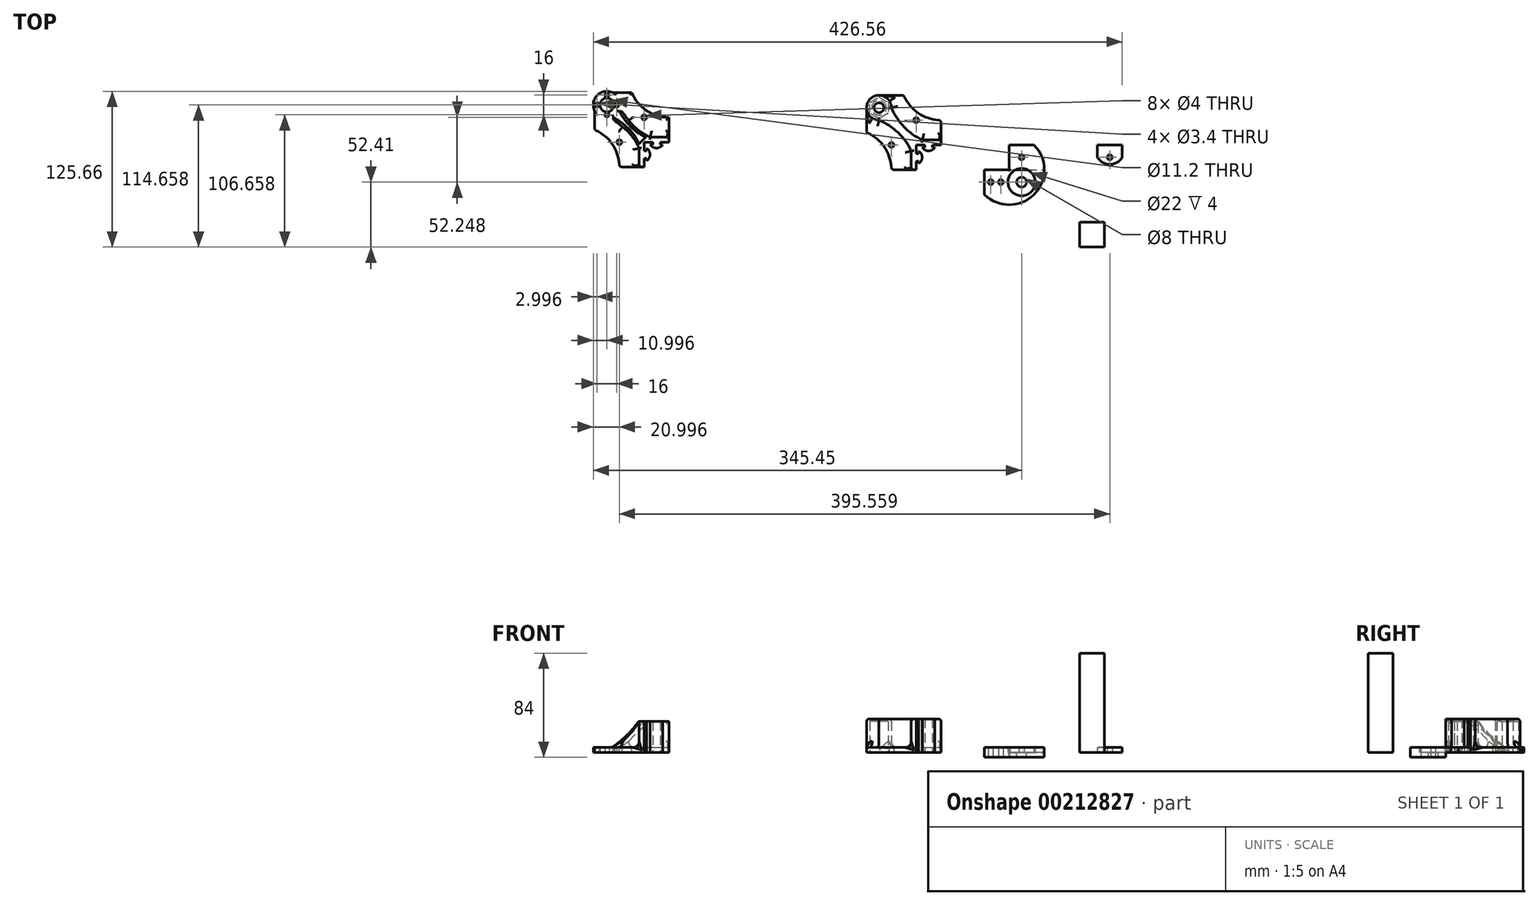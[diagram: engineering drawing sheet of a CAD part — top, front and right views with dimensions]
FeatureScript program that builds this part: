
annotation { "Feature Type Name" : "Feature", "Feature Type Description" : "" }
export const myFeature = defineFeature(function(context is Context, id is Id, definition is map)
    precondition{}
    {
        {
            var Q0;
            Q0=qCreatedBy(makeId("Top.planeOp"),FACE);
            var sketch = newSketch(context, id + "F0", { "sketchPlane" : qUnion([Q0])});
            skLineSegment(sketch, "E0.top", {"start": v(9.5, -10) * mm, "end": v(-10, -10) * mm});
            skLineSegment(sketch, "E0.left", {"start": v(10, 10) * mm, "end": v(10, -9.5) * mm});
            skPoint(sketch, "E0.middle", {"position": v(0, 0) * mm});
            skLineSegment(sketch, "E1.bottom", {"start": v(-10, -10) * mm, "end": v(-30, -10) * mm});
            skLineSegment(sketch, "E1.top", {"start": v(-10, -30) * mm, "end": v(-30, -30) * mm});
            skLineSegment(sketch, "E1.left", {"start": v(-10, -10) * mm, "end": v(-10, -30) * mm});
            skLineSegment(sketch, "E1.right", {"start": v(-30, -10) * mm, "end": v(-30, -30) * mm});
            skLineSegment(sketch, "E2.bottom", {"start": v(10, 10) * mm, "end": v(30, 10) * mm, "construction": true});
            skLineSegment(sketch, "E2.top", {"start": v(10, 30) * mm, "end": v(30, 30) * mm});
            skLineSegment(sketch, "E2.left", {"start": v(10, 10) * mm, "end": v(10, 30) * mm});
            skLineSegment(sketch, "E2.right", {"start": v(30, 10) * mm, "end": v(30, 30) * mm});
            skLineSegment(sketch, "E3", {"start": v(-10, -30) * mm, "end": v(10, -30) * mm});
            skLineSegment(sketch, "E4", {"start": v(10, -10) * mm, "end": v(30, -30) * mm, "construction": true});
            skCircle(sketch, "E5", {"center": v(20, -20) * mm, "radius": 4 * mm});
            skCircle(sketch, "E6", {"center": v(20, -20) * mm, "radius": 11 * mm});
            skLineSegment(sketch, "E7", {"start": v(-10, -30) * mm, "end": v(-30, -10) * mm, "construction": true});
            skLineSegment(sketch, "E8", {"start": v(30, 10) * mm, "end": v(10, 30) * mm, "construction": true});
            skCircle(sketch, "E9", {"center": v(20, 20) * mm, "radius": 2 * mm});
            skCircle(sketch, "E10", {"center": v(-20, -20) * mm, "radius": 2 * mm});
            skLineSegment(sketch, "E11", {"start": v(30, -10) * mm, "end": v(30, 10) * mm});
            skArc(sketch, "E12", {"start": v(10, -30) * mm, "mid": v(30, -30) * mm, "end": v(30, -10) * mm, "construction": true});
            skArc(sketch, "E13", {"start": v(9.5, -10) * mm, "mid": v(10.35, -10.35) * mm, "end": v(10, -9.5) * mm});
            skCircle(sketch, "E14", {"center": v(20, 0) * mm, "radius": 2 * mm});
            skPoint(sketch, "E14.centerSnap0", {"position": v(20, 10) * mm});
            skCircle(sketch, "E15", {"center": v(3.25, -20) * mm, "radius": 2 * mm});
            skPoint(sketch, "E15.centerSnap0", {"position": v(-10, -20) * mm});
            skLineSegment(sketch, "E16", {"start": v(55.55, 30) * mm, "end": v(55.55, -7.44) * mm, "construction": true});
            skLineSegment(sketch, "E17.MirrorCS", {"start": v(81.1, 0.25) * mm, "end": v(81.1, 10) * mm});
            skCircle(sketch, "E18.MirrorC", {"center": v(91.1, 0) * mm, "radius": 2 * mm});
            skLineSegment(sketch, "E19.MirrorCS", {"start": v(81.1, 10) * mm, "end": v(81.1, 30) * mm, "construction": true});
            skLineSegment(sketch, "E20.MirrorCS", {"start": v(101.1, 0.25) * mm, "end": v(101.1, 30) * mm});
            skLineSegment(sketch, "E21.MirrorCS", {"start": v(101.1, 30) * mm, "end": v(81.1, 30) * mm, "construction": true});
            skCircle(sketch, "E22.MirrorC", {"center": v(91.1, 20) * mm, "radius": 2 * mm});
            skArc(sketch, "E23", {"start": v(81.1, 0.25) * mm, "mid": v(91.1, -5.73) * mm, "end": v(101.1, 0.25) * mm});
            skPoint(sketch, "E24.MirrorCS.start.orphan", {"position": v(101.1, 10) * mm});
            skLineSegment(sketch, "E25.left", {"start": v(-3, 8) * mm, "end": v(-3, 10) * mm});
            skLineSegment(sketch, "E25.right", {"start": v(3, 8) * mm, "end": v(3, 10) * mm});
            skPoint(sketch, "E25.middle", {"position": v(0, 11) * mm});
            skPoint(sketch, "E26.middle", {"position": v(-10, 0) * mm});
            skPoint(sketch, "E25.top.end.orphan", {"position": v(3, 14) * mm});
            skPoint(sketch, "E25.top.start.orphan", {"position": v(-3, 14) * mm});
            skPoint(sketch, "E26.right.end.orphan", {"position": v(-14, 3) * mm});
            skPoint(sketch, "E26.right.start.orphan", {"position": v(-13, -3) * mm});
            skLineSegment(sketch, "E27", {"start": v(3, 8) * mm, "end": v(5, 8) * mm});
            skLineSegment(sketch, "E28", {"start": v(-3, 8) * mm, "end": v(-5, 8) * mm});
            skPoint(sketch, "E29.orphan", {"position": v(0, 8) * mm});
            skArc(sketch, "E30", {"start": v(-5, 8) * mm, "mid": v(0, 5.2) * mm, "end": v(5, 8) * mm});
            skLineSegment(sketch, "E31", {"start": v(3, 10) * mm, "end": v(10, 10) * mm});
            skLineSegment(sketch, "E32", {"start": v(-3, 10) * mm, "end": v(-10, 10) * mm});
            skLineSegment(sketch, "E33", {"start": v(-10, -10) * mm, "end": v(-10, -3) * mm});
            skLineSegment(sketch, "E34", {"start": v(-10, 3) * mm, "end": v(-10, 10) * mm});
            skLineSegment(sketch, "E35", {"start": v(-10, 10) * mm, "end": v(-30, 30) * mm, "construction": true});
            skCircle(sketch, "E36", {"center": v(0, 20) * mm, "radius": 2 * mm, "construction": true});
            skCircle(sketch, "E37", {"center": v(-20, 0) * mm, "radius": 2 * mm, "construction": true});
            skLineSegment(sketch, "E38.1.0", {"start": v(-8, 3) * mm, "end": v(-10, 3) * mm});
            skLineSegment(sketch, "E38.1.1", {"start": v(-8, 3) * mm, "end": v(-8, 5) * mm});
            skArc(sketch, "E38.1.2", {"start": v(-8, -5) * mm, "mid": v(-5.2, 0) * mm, "end": v(-8, 5) * mm});
            skLineSegment(sketch, "E38.1.3", {"start": v(-8, -3) * mm, "end": v(-10, -3) * mm});
            skLineSegment(sketch, "E38.1.4", {"start": v(-8, -3) * mm, "end": v(-8, -5) * mm});
            skLineSegment(sketch, "E38.anchor1", {"start": v(0, 0) * mm, "end": v(-5, 8) * mm, "construction": true});
            skLineSegment(sketch, "E38.anchor2", {"start": v(0, 0) * mm, "end": v(-8, -5) * mm, "construction": true});
            skLineSegment(sketch, "E39", {"start": v(10, 14) * mm, "end": v(-5.03, 14) * mm});
            skLineSegment(sketch, "E40", {"start": v(-14, 5.03) * mm, "end": v(-14, -10) * mm});
            skPoint(sketch, "E41.orphan", {"position": v(-14, 14) * mm});
            skPoint(sketch, "E42.visualSharp", {"position": v(-12, 14) * mm});
            skPoint(sketch, "E43.visualSharp", {"position": v(-14, 12.86) * mm});
            skLineSegment(sketch, "E44.bottom", {"start": v(66.82, -52.41) * mm, "end": v(86.82, -52.41) * mm});
            skLineSegment(sketch, "E44.top", {"start": v(66.82, -72.41) * mm, "end": v(86.82, -72.41) * mm});
            skLineSegment(sketch, "E44.left", {"start": v(66.82, -52.41) * mm, "end": v(66.82, -72.41) * mm});
            skLineSegment(sketch, "E44.right", {"start": v(86.82, -52.41) * mm, "end": v(86.82, -72.41) * mm});
            skPoint(sketch, "E44.middle", {"position": v(76.82, -62.41) * mm});
            skLineSegment(sketch, "E45", {"start": v(30, 10) * mm, "end": v(10, 10) * mm});
            skLineSegment(sketch, "E46", {"start": v(9.5, -10) * mm, "end": v(38.28, -10) * mm});
            skLineSegment(sketch, "E47", {"start": v(-30, -10) * mm, "end": v(-50, -10) * mm});
            skLineSegment(sketch, "E48", {"start": v(10, 30) * mm, "end": v(10, 50) * mm});
            skLineSegment(sketch, "E49", {"start": v(10, 50) * mm, "end": v(-50, 50) * mm});
            skLineSegment(sketch, "E50", {"start": v(-50, -10) * mm, "end": v(-50, 50) * mm});
            skLineSegment(sketch, "E51", {"start": v(-30, 30) * mm, "end": v(-50, 50) * mm, "construction": true});
            skCircle(sketch, "E52.cCircle", {"center": v(-40, 40) * mm, "radius": 8.75 * mm, "construction": true});
            skPoint(sketch, "E52.cCircle.perimeterSnap0", {"position": v(-40, 40) * mm});
            skLineSegment(sketch, "E52.0", {"start": v(-40, 31.25) * mm, "end": v(-47.57, 35.63) * mm});
            skPoint(sketch, "E52.0.startSnap0", {"position": v(-40, 40) * mm});
            skLineSegment(sketch, "E52.1", {"start": v(-47.57, 35.63) * mm, "end": v(-47.57, 44.37) * mm});
            skLineSegment(sketch, "E52.2", {"start": v(-47.57, 44.37) * mm, "end": v(-40, 48.75) * mm});
            skLineSegment(sketch, "E52.3", {"start": v(-40, 48.75) * mm, "end": v(-32.43, 44.37) * mm});
            skLineSegment(sketch, "E52.4", {"start": v(-32.43, 44.37) * mm, "end": v(-32.43, 35.63) * mm});
            skLineSegment(sketch, "E52.5", {"start": v(-32.43, 35.63) * mm, "end": v(-40, 31.25) * mm});
            skCircle(sketch, "E53", {"center": v(-40, 40) * mm, "radius": 4 * mm});
            skArc(sketch, "E54", {"start": v(-32.93, 32.93) * mm, "mid": v(-43.83, 49.24) * mm, "end": v(-40, 30) * mm});
            skArc(sketch, "E55", {"start": v(-14, 5.03) * mm, "mid": v(-24.66, 19.96) * mm, "end": v(-40, 30) * mm});
            skArc(sketch, "E56.MirrorCS", {"start": v(-5.03, 14) * mm, "mid": v(-19.96, 24.66) * mm, "end": v(-30, 40) * mm});
            skLineSegment(sketch, "E57", {"start": v(101.1, 10) * mm, "end": v(81.1, 10) * mm});
            skArc(sketch, "E58", {"start": v(-20, 50) * mm, "mid": v(-8.03, 35.46) * mm, "end": v(10, 30) * mm});
            skArc(sketch, "E59", {"start": v(-30, -10) * mm, "mid": v(-35.46, 8.03) * mm, "end": v(-50, 20) * mm});
            skLineSegment(sketch, "E60", {"start": v(-30, -10) * mm, "end": v(-30, 30) * mm, "construction": true});
            skLineSegment(sketch, "E61", {"start": v(10, 30) * mm, "end": v(-30, 30) * mm, "construction": true});
            skCircle(sketch, "E62", {"center": v(-30, 10) * mm, "radius": 2 * mm});
            skCircle(sketch, "E63", {"center": v(-10, 30) * mm, "radius": 2 * mm});
            skArc(sketch, "E64", {"start": v(-10, -30) * mm, "mid": v(30, -30) * mm, "end": v(30, 10) * mm});
            skPoint(sketch, "E65.middle", {"position": v(-274.45, 2.25) * mm});
            skLineSegment(sketch, "E66.bottom", {"start": v(-284.45, -7.75) * mm, "end": v(-304.45, -7.75) * mm});
            skLineSegment(sketch, "E67.left", {"start": v(-277.45, 10.25) * mm, "end": v(-277.45, 12.25) * mm});
            skLineSegment(sketch, "E67.right", {"start": v(-271.45, 10.25) * mm, "end": v(-271.45, 12.25) * mm});
            skPoint(sketch, "E67.middle", {"position": v(-274.45, 13.25) * mm});
            skPoint(sketch, "E68.middle", {"position": v(-284.45, 2.25) * mm});
            skPoint(sketch, "E67.top.end.orphan", {"position": v(-271.45, 16.25) * mm});
            skPoint(sketch, "E67.top.start.orphan", {"position": v(-277.45, 16.25) * mm});
            skPoint(sketch, "E68.right.end.orphan", {"position": v(-288.45, 5.25) * mm});
            skPoint(sketch, "E68.right.start.orphan", {"position": v(-287.45, -0.75) * mm});
            skLineSegment(sketch, "E69", {"start": v(-271.45, 10.25) * mm, "end": v(-269.45, 10.25) * mm});
            skLineSegment(sketch, "E70", {"start": v(-277.45, 10.25) * mm, "end": v(-279.45, 10.25) * mm});
            skPoint(sketch, "E71.orphan", {"position": v(-274.45, 10.25) * mm});
            skArc(sketch, "E72", {"start": v(-279.45, 10.25) * mm, "mid": v(-274.45, 7.45) * mm, "end": v(-269.45, 10.25) * mm});
            skLineSegment(sketch, "E73", {"start": v(-277.45, 12.25) * mm, "end": v(-284.45, 12.25) * mm});
            skLineSegment(sketch, "E74", {"start": v(-284.45, 5.25) * mm, "end": v(-284.45, 12.25) * mm});
            skLineSegment(sketch, "E75", {"start": v(-284.45, 12.25) * mm, "end": v(-304.45, 32.25) * mm, "construction": true});
            skCircle(sketch, "E76", {"center": v(-274.45, 22.25) * mm, "radius": 2 * mm, "construction": true});
            skCircle(sketch, "E77", {"center": v(-294.45, 2.25) * mm, "radius": 2 * mm, "construction": true});
            skLineSegment(sketch, "E78.1.0", {"start": v(-282.45, 5.25) * mm, "end": v(-284.45, 5.25) * mm});
            skLineSegment(sketch, "E78.1.1", {"start": v(-282.45, 5.25) * mm, "end": v(-282.45, 7.25) * mm});
            skArc(sketch, "E78.1.2", {"start": v(-282.45, -2.75) * mm, "mid": v(-279.66, 2.25) * mm, "end": v(-282.45, 7.25) * mm});
            skLineSegment(sketch, "E78.1.3", {"start": v(-282.45, -0.75) * mm, "end": v(-284.45, -0.75) * mm});
            skLineSegment(sketch, "E78.1.4", {"start": v(-282.45, -0.75) * mm, "end": v(-282.45, -2.75) * mm});
            skLineSegment(sketch, "E78.anchor1", {"start": v(-274.45, 2.25) * mm, "end": v(-279.45, 10.25) * mm, "construction": true});
            skLineSegment(sketch, "E78.anchor2", {"start": v(-274.45, 2.25) * mm, "end": v(-282.45, -2.75) * mm, "construction": true});
            skLineSegment(sketch, "E79", {"start": v(-264.45, 16.25) * mm, "end": v(-279.49, 16.25) * mm});
            skLineSegment(sketch, "E80", {"start": v(-288.45, 7.28) * mm, "end": v(-288.45, -7.75) * mm});
            skPoint(sketch, "E81.orphan", {"position": v(-288.45, 16.25) * mm});
            skPoint(sketch, "E82.visualSharp", {"position": v(-286.45, 16.25) * mm});
            skPoint(sketch, "E83.visualSharp", {"position": v(-288.45, 15.1) * mm});
            skLineSegment(sketch, "E84", {"start": v(-304.45, -7.75) * mm, "end": v(-324.45, -7.75) * mm});
            skLineSegment(sketch, "E85", {"start": v(-264.45, 52.25) * mm, "end": v(-309.87, 52.25) * mm});
            skLineSegment(sketch, "E86", {"start": v(-324.45, -7.75) * mm, "end": v(-324.45, 37.67) * mm});
            skLineSegment(sketch, "E87", {"start": v(-304.45, 32.25) * mm, "end": v(-324.45, 52.25) * mm, "construction": true});
            skCircle(sketch, "E88.cCircle", {"center": v(-314.45, 42.25) * mm, "radius": 8 * mm, "construction": true});
            skPoint(sketch, "E88.cCircle.perimeterSnap0", {"position": v(-314.45, 42.25) * mm});
            skPoint(sketch, "E88.0.startSnap0", {"position": v(-314.45, 42.25) * mm});
            skCircle(sketch, "E89", {"center": v(-314.45, 42.25) * mm, "radius": 5.6 * mm});
            skArc(sketch, "E90", {"start": v(-294.45, 52.25) * mm, "mid": v(-282.48, 37.7) * mm, "end": v(-264.45, 32.25) * mm});
            skArc(sketch, "E91", {"start": v(-304.45, -7.75) * mm, "mid": v(-309.91, 10.28) * mm, "end": v(-324.45, 22.25) * mm});
            skCircle(sketch, "E92", {"center": v(-304.45, 12.25) * mm, "radius": 2 * mm});
            skCircle(sketch, "E93", {"center": v(-284.45, 32.25) * mm, "radius": 2 * mm});
            skLineSegment(sketch, "E94", {"start": v(-271.45, 12.25) * mm, "end": v(-264.45, 12.25) * mm});
            skLineSegment(sketch, "E95", {"start": v(-264.45, 12.25) * mm, "end": v(-264.45, 16.25) * mm});
            skLineSegment(sketch, "E96", {"start": v(-284.45, -7.75) * mm, "end": v(-284.45, -0.75) * mm});
            skLineSegment(sketch, "E97", {"start": v(-264.45, 16.25) * mm, "end": v(-264.45, 32.25) * mm});
            skArc(sketch, "E98", {"start": v(-303.45, 42.17) * mm, "mid": v(-322.23, 50.03) * mm, "end": v(-314.38, 31.25) * mm});
            skCircle(sketch, "E99", {"center": v(-314.45, 50.25) * mm, "radius": 1.7 * mm});
            skCircle(sketch, "E100", {"center": v(-322.45, 42.25) * mm, "radius": 1.7 * mm});
            skCircle(sketch, "E101", {"center": v(-314.45, 34.25) * mm, "radius": 1.7 * mm});
            skCircle(sketch, "E102", {"center": v(-306.45, 42.25) * mm, "radius": 1.7 * mm});
            skArc(sketch, "E103", {"start": v(-288.45, 7.28) * mm, "mid": v(-298.86, 22.03) * mm, "end": v(-314.38, 31.25) * mm});
            skArc(sketch, "E104.MirrorCS", {"start": v(-279.49, 16.25) * mm, "mid": v(-294.24, 26.65) * mm, "end": v(-303.45, 42.17) * mm});
            skLineSegment(sketch, "E105.trimOffspring", {"start": v(-324.45, 46.83) * mm, "end": v(-324.45, 52.25) * mm});
            skLineSegment(sketch, "E106.trimOffspring", {"start": v(-319.04, 52.25) * mm, "end": v(-324.45, 52.25) * mm});
            skArc(sketch, "E107", {"start": v(-314.38, 31.25) * mm, "mid": v(-307, 34.8) * mm, "end": v(-303.45, 42.17) * mm});
            skCircle(sketch, "E108", {"center": v(-4.93, -20) * mm, "radius": 2 * mm});
            skSolve(sketch);
        }
        {
            var Q0;
            Q0=makeQuery(id+"F0.imprint","IMPRINT",FACE,{"disambiguationData":[TD([[makeQuery(id+"F0.imprint","IMPRINT",EDGE,{"derivedFrom":sQuery(id+"F0.wireOp",EDGE,"E0.top")}),1.0]])]});
            var Q1;
            Q1=makeQuery(id+"F0.imprint","IMPRINT",FACE,{"disambiguationData":[TD([[makeQuery(id+"F0.imprint","IMPRINT",EDGE,{"derivedFrom":sQuery(id+"F0.wireOp",EDGE,"E17.MirrorCS")}),-1.0]])]});
            var Q2;
            {var subQ1=sQuery(id+"F0.wireOp",EDGE,"E0.left");Q2=makeQuery(id+"F0.imprint","IMPRINT",FACE,{"disambiguationData":[TD([[makeQuery(id+"F0.imprint","IMPRINT",EDGE,{"derivedFrom":subQ1}),1.0]])]});}
            var Q3;
            {var subQ0=sQuery(id+"F0.wireOp",EDGE,"E11");Q3=makeQuery(id+"F0.imprint","IMPRINT",FACE,{"disambiguationData":[TD([[makeQuery(id+"F0.imprint","IMPRINT",EDGE,{"derivedFrom":subQ0}),-1.0]])]});}
            extrude(context, id + "F1", {"entities" : qUnion([Q0, Q1, Q2, Q3]), "depth" : 4 * mm});
        }
        {
            var Q0;
            Q0=makeQuery(id+"F0.imprint","IMPRINT",FACE,{"disambiguationData":[TD([[makeQuery(id+"F0.imprint","IMPRINT",EDGE,{"derivedFrom":sQuery(id+"F0.wireOp",EDGE,"E0.top")}),1.0]])]});
            var Q1;
            Q1=makeQuery(id+"F0.imprint","IMPRINT",FACE,{"disambiguationData":[TD([[makeQuery(id+"F0.imprint","IMPRINT",EDGE,{"derivedFrom":sQuery(id+"F0.wireOp",EDGE,"E5")}),-1.0]])]});
            extrude(context, id + "F2", {"entities" : qUnion([Q0, Q1]), "oppositeDirection" : true, "depth" : 4 * mm});
        }
        {
            var Q0;
            Q0=makeQuery(id+"F0.imprint","IMPRINT",FACE,{"disambiguationData":[TD([[makeQuery(id+"F0.imprint","IMPRINT",EDGE,{"derivedFrom":sQuery(id+"F0.wireOp",EDGE,"E36")}),-1.0]])]});
            var Q1;
            Q1=makeQuery(id+"F0.imprint","IMPRINT",FACE,{"disambiguationData":[TD([[makeQuery(id+"F0.imprint","IMPRINT",EDGE,{"derivedFrom":sQuery(id+"F0.wireOp",EDGE,"E37")}),-1.0]])]});
            var Q2;
            {var subQ5=sQuery(id+"F0.wireOp",EDGE,"E39");Q2=makeQuery(id+"F0.imprint","IMPRINT",FACE,{"disambiguationData":[TD([[makeQuery(id+"F0.imprint","IMPRINT",EDGE,{"derivedFrom":subQ5}),-1.0]])]});}
            var Q3;
            {var subQ4=sQuery(id+"F0.wireOp",EDGE,"E40");Q3=makeQuery(id+"F0.imprint","IMPRINT",FACE,{"disambiguationData":[TD([[makeQuery(id+"F0.imprint","IMPRINT",EDGE,{"derivedFrom":subQ4}),-1.0]])]});}
            var Q4;
            Q4=makeQuery(id+"F0.imprint","IMPRINT",FACE,{"disambiguationData":[TD([[makeQuery(id+"F0.imprint","IMPRINT",EDGE,{"derivedFrom":sQuery(id+"F0.wireOp",EDGE,"E25.left")}),-1.0]])]});
            var Q5;
            {var subQ1=sQuery(id+"F0.wireOp",EDGE,"E80");Q5=makeQuery(id+"F0.imprint","IMPRINT",FACE,{"disambiguationData":[TD([[makeQuery(id+"F0.imprint","IMPRINT",EDGE,{"derivedFrom":subQ1}),-1.0]])]});}
            var Q6;
            Q6=makeQuery(id+"F0.imprint","IMPRINT",FACE,{"disambiguationData":[TD([[makeQuery(id+"F0.imprint","IMPRINT",EDGE,{"derivedFrom":sQuery(id+"F0.wireOp",EDGE,"E67.left")}),-1.0]])]});
            var Q7;
            Q7=makeQuery(id+"F0.imprint","IMPRINT",FACE,{"disambiguationData":[TD([[makeQuery(id+"F0.imprint","IMPRINT",EDGE,{"derivedFrom":sQuery(id+"F0.wireOp",EDGE,"E79")}),-1.0]])]});
            var Q8;
            Q8=makeQuery(id+"F0.imprint","IMPRINT",FACE,{"disambiguationData":[TD([[makeQuery(id+"F0.imprint","IMPRINT",EDGE,{"derivedFrom":sQuery(id+"F0.wireOp",EDGE,"E89")}),-1.0]])]});
            extrude(context, id + "F3", {"entities" : qUnion([Q0, Q1, Q2, Q3, Q4, Q5, Q6, Q7, Q8]), "depth" : 4 * mm});
        }
        {
            var Q0;
            Q0=makeQuery(id+"F0.imprint","IMPRINT",FACE,{"disambiguationData":[TD([[makeQuery(id+"F0.imprint","IMPRINT",EDGE,{"derivedFrom":sQuery(id+"F0.wireOp",EDGE,"E25.left")}),-1.0]])]});
            extrude(context, id + "F4", {"entities" : qUnion([Q0]), "operationType" : NewBodyOperationType.ADD, "depth" : 25 * mm});
        }
        {
            var Q0;
            Q0=makeQuery(id+"F0.imprint","IMPRINT",FACE,{"disambiguationData":[TD([[makeQuery(id+"F0.imprint","IMPRINT",EDGE,{"derivedFrom":sQuery(id+"F0.wireOp",EDGE,"E25.left")}),-1.0]])]});
            var Q1;
            Q1=makeQuery(id+"F0.imprint","IMPRINT",FACE,{"disambiguationData":[TD([[makeQuery(id+"F0.imprint","IMPRINT",EDGE,{"derivedFrom":sQuery(id+"F0.wireOp",EDGE,"G3BymW2v-wqTc-e0WK-M3na-BjgTxJpdWQWx")}),-1.0]])]});
            var Q2;
            Q2=makeQuery(id+"F0.imprint","IMPRINT",FACE,{"disambiguationData":[TD([[makeQuery(id+"F0.imprint","IMPRINT",EDGE,{"derivedFrom":sQuery(id+"F0.wireOp",EDGE,"E52.0")}),-1.0]])]});
            extrude(context, id + "F5", {"entities" : qUnion([Q0, Q1, Q2]), "operationType" : NewBodyOperationType.ADD, "depth" : 27 * mm, "hasSecondDirection" : true, "secondDirectionOppositeDirection" : false, "secondDirectionDepth" : 25 * mm});
        }
        {
            var Q0;
            Q0=makeQuery(id+"F0.imprint","IMPRINT",FACE,{"disambiguationData":[TD([[makeQuery(id+"F0.imprint","IMPRINT",EDGE,{"derivedFrom":sQuery(id+"F0.wireOp",EDGE,"E67.left")}),-1.0]])]});
            extrude(context, id + "F6", {"entities" : qUnion([Q0]), "operationType" : NewBodyOperationType.ADD, "depth" : 25 * mm});
        }
        {
            var Q0;
            Q0=makeQuery(id+"F3.opExtrude","SWEPT_BODY",BODY,{"disambiguationData":[OSD([sQuery(id+"F0.wireOp",EDGE,"E1.bottom"),sQuery(id+"F0.wireOp",EDGE,"E2.left"),sQuery(id+"F0.wireOp",EDGE,"E25.left"),sQuery(id+"F0.wireOp",EDGE,"E25.right"),sQuery(id+"F0.wireOp",EDGE,"E27"),sQuery(id+"F0.wireOp",EDGE,"E28"),sQuery(id+"F0.wireOp",EDGE,"E30"),sQuery(id+"F0.wireOp",EDGE,"E31"),sQuery(id+"F0.wireOp",EDGE,"E32"),sQuery(id+"F0.wireOp",EDGE,"E33"),sQuery(id+"F0.wireOp",EDGE,"E34"),sQuery(id+"F0.wireOp",EDGE,"E38.1.0"),sQuery(id+"F0.wireOp",EDGE,"E38.1.1"),sQuery(id+"F0.wireOp",EDGE,"E38.1.2"),sQuery(id+"F0.wireOp",EDGE,"E38.1.3"),sQuery(id+"F0.wireOp",EDGE,"E38.1.4"),sQuery(id+"F0.wireOp",EDGE,"E49"),sQuery(id+"F0.wireOp",EDGE,"E50"),sQuery(id+"F0.wireOp",EDGE,"E52.0"),sQuery(id+"F0.wireOp",EDGE,"E52.1"),sQuery(id+"F0.wireOp",EDGE,"E52.2"),sQuery(id+"F0.wireOp",EDGE,"E52.3"),sQuery(id+"F0.wireOp",EDGE,"E52.4"),sQuery(id+"F0.wireOp",EDGE,"E52.5"),sQuery(id+"F0.wireOp",EDGE,"E54"),sQuery(id+"F0.wireOp",EDGE,"E58"),sQuery(id+"F0.wireOp",EDGE,"E59"),sQuery(id+"F0.wireOp",EDGE,"E62"),sQuery(id+"F0.wireOp",EDGE,"E63")])]});
            transform(context, id + "F7", {"entities" : qUnion([Q0]), "transformType" : TransformType.TRANSLATION_3D, "dx" : -55 * mm, "dy" : 0 * mm, "dz" : 0 * mm, "makeCopy" : false});
        }
        {
            var Q0;
            Q0=makeQuery(id+"F5.opExtrude","CAP_EDGE",EDGE,{"disambiguationData":[OSD([sQuery(id+"F0.wireOp",EDGE,"E53")])],"isStart":true});
            chamfer(context, id + "F8", {"entities" : qUnion([Q0]), "width" : 2 * mm, "tangentPropagation" : true});
        }
        {
            var Q0;
            Q0=makeQuery(id+"F6.opExtrude","CAP_EDGE",EDGE,{"disambiguationData":[OSD([sQuery(id+"F0.wireOp",EDGE,"E107")])],"isStart":false});
            chamfer(context, id + "F9", {"entities" : qUnion([Q0]), "chamferType" : ChamferType.TWO_OFFSETS, "width1" : 21 * mm, "oppositeDirection" : false, "width2" : 30 * mm, "tangentPropagation" : true});
        }
        {
            var Q0;
            Q0=makeQuery(id+"F5.opExtrude","CAP_EDGE",EDGE,{"disambiguationData":[OSD([sQuery(id+"F0.wireOp",EDGE,"E56.MirrorCS")])],"isStart":false});
            var Q1;
            Q1=makeQuery(id+"F5.opExtrude","CAP_EDGE",EDGE,{"disambiguationData":[OSD([sQuery(id+"F0.wireOp",EDGE,"E39")])],"isStart":false});
            var Q2;
            Q2=makeQuery(id+"F5.opExtrude","CAP_EDGE",EDGE,{"disambiguationData":[OSD([sQuery(id+"F0.wireOp",EDGE,"E2.left")])],"isStart":false});
            var Q3;
            Q3=makeQuery(id+"F5.opExtrude","CAP_EDGE",EDGE,{"disambiguationData":[OSD([sQuery(id+"F0.wireOp",EDGE,"E55")])],"isStart":false});
            var Q4;
            Q4=makeQuery(id+"F5.opExtrude","CAP_EDGE",EDGE,{"disambiguationData":[OSD([sQuery(id+"F0.wireOp",EDGE,"E40")])],"isStart":false});
            var Q5;
            Q5=makeQuery(id+"F5.opExtrude","CAP_EDGE",EDGE,{"disambiguationData":[OSD([sQuery(id+"F0.wireOp",EDGE,"E54")])],"isStart":false});
            var Q6;
            {var subQ0=sQuery(id+"F0.wireOp",EDGE,"E39");var subQ1=sQuery(id+"F0.wireOp",EDGE,"E2.left");Q6=makeQuery(id+"F5.boolean.opBoolean","MERGE",EDGE,{"derivedFrom":[makeQuery(id+"F4.opExtrude","SWEPT_EDGE",EDGE,{"disambiguationData":[OSD([subQ1,subQ0])]}),makeQuery(id+"F5.opExtrude","SWEPT_EDGE",EDGE,{"disambiguationData":[OSD([subQ1,subQ0])]})]});}
            var Q7;
            {var subQ0=sQuery(id+"F0.wireOp",EDGE,"E40");var subQ1=sQuery(id+"F0.wireOp",EDGE,"E1.bottom");Q7=makeQuery(id+"F5.boolean.opBoolean","MERGE",EDGE,{"derivedFrom":[makeQuery(id+"F4.opExtrude","SWEPT_EDGE",EDGE,{"disambiguationData":[OSD([subQ1,subQ0])]}),makeQuery(id+"F5.opExtrude","SWEPT_EDGE",EDGE,{"disambiguationData":[OSD([subQ1,subQ0])]})]});}
            var Q8;
            Q8=makeQuery(id+"F3.opExtrude","CAP_EDGE",EDGE,{"disambiguationData":[OSD([sQuery(id+"F0.wireOp",EDGE,"E1.bottom"),sQuery(id+"F0.wireOp",EDGE,"E47")])],"isStart":false});
            var Q9;
            Q9=makeQuery(id+"F3.opExtrude","CAP_EDGE",EDGE,{"disambiguationData":[OSD([sQuery(id+"F0.wireOp",EDGE,"E50")])],"isStart":false});
            var Q10;
            Q10=makeQuery(id+"F3.opExtrude","SWEPT_EDGE",EDGE,{"disambiguationData":[OSD([sQuery(id+"F0.wireOp",EDGE,"E47"),sQuery(id+"F0.wireOp",EDGE,"E50")])]});
            var Q11;
            Q11=makeQuery(id+"F3.opExtrude","CAP_EDGE",EDGE,{"disambiguationData":[OSD([sQuery(id+"F0.wireOp",EDGE,"E2.left"),sQuery(id+"F0.wireOp",EDGE,"E48")])],"isStart":false});
            var Q12;
            Q12=makeQuery(id+"F3.opExtrude","CAP_EDGE",EDGE,{"disambiguationData":[OSD([sQuery(id+"F0.wireOp",EDGE,"E49")])],"isStart":false});
            var Q13;
            Q13=makeQuery(id+"F3.opExtrude","SWEPT_EDGE",EDGE,{"disambiguationData":[OSD([sQuery(id+"F0.wireOp",EDGE,"E48"),sQuery(id+"F0.wireOp",EDGE,"E49")])]});
            var Q14;
            Q14=makeQuery(id+"F3.opExtrude","CAP_EDGE",EDGE,{"disambiguationData":[OSD([sQuery(id+"F0.wireOp",EDGE,"E58")])],"isStart":false});
            var Q15;
            Q15=makeQuery(id+"F3.opExtrude","SWEPT_EDGE",EDGE,{"disambiguationData":[OSD([sQuery(id+"F0.wireOp",EDGE,"E2.top"),sQuery(id+"F0.wireOp",EDGE,"E2.left"),sQuery(id+"F0.wireOp",EDGE,"E48"),sQuery(id+"F0.wireOp",EDGE,"E58")])]});
            var Q16;
            Q16=makeQuery(id+"F3.opExtrude","SWEPT_EDGE",EDGE,{"disambiguationData":[OSD([sQuery(id+"F0.wireOp",EDGE,"E1.bottom"),sQuery(id+"F0.wireOp",EDGE,"E1.right"),sQuery(id+"F0.wireOp",EDGE,"E47"),sQuery(id+"F0.wireOp",EDGE,"E59")])]});
            var Q17;
            Q17=makeQuery(id+"F3.opExtrude","CAP_EDGE",EDGE,{"disambiguationData":[OSD([sQuery(id+"F0.wireOp",EDGE,"E59")])],"isStart":false});
            fillet(context, id + "F10", {"entities" : qUnion([Q0, Q1, Q2, Q3, Q4, Q5, Q6, Q7, Q8, Q9, Q10, Q11, Q12, Q13, Q14, Q15, Q16, Q17]), "radius" : 2 * mm, "tangentPropagation" : true, "allowEdgeOverflow" : false});
        }
        {
            var Q0;
            Q0=makeQuery(id+"F4.boolean.opBoolean","INTERSECT",EDGE,{"derivedFrom":[makeQuery(id+"F3.opExtrude","CAP_FACE",FACE,{"disambiguationData":[OSD([sQuery(id+"F0.wireOp",EDGE,"E1.bottom"),sQuery(id+"F0.wireOp",EDGE,"E2.left"),sQuery(id+"F0.wireOp",EDGE,"E25.left"),sQuery(id+"F0.wireOp",EDGE,"E25.right"),sQuery(id+"F0.wireOp",EDGE,"E27"),sQuery(id+"F0.wireOp",EDGE,"E28"),sQuery(id+"F0.wireOp",EDGE,"E30"),sQuery(id+"F0.wireOp",EDGE,"E31"),sQuery(id+"F0.wireOp",EDGE,"E32"),sQuery(id+"F0.wireOp",EDGE,"E33"),sQuery(id+"F0.wireOp",EDGE,"E34"),sQuery(id+"F0.wireOp",EDGE,"E36"),sQuery(id+"F0.wireOp",EDGE,"E37"),sQuery(id+"F0.wireOp",EDGE,"E38.1.0"),sQuery(id+"F0.wireOp",EDGE,"E38.1.1"),sQuery(id+"F0.wireOp",EDGE,"E38.1.2"),sQuery(id+"F0.wireOp",EDGE,"E38.1.3"),sQuery(id+"F0.wireOp",EDGE,"E38.1.4"),sQuery(id+"F0.wireOp",EDGE,"E47"),sQuery(id+"F0.wireOp",EDGE,"E48"),sQuery(id+"F0.wireOp",EDGE,"E49"),sQuery(id+"F0.wireOp",EDGE,"E50"),sQuery(id+"F0.wireOp",EDGE,"E52.0"),sQuery(id+"F0.wireOp",EDGE,"E52.1"),sQuery(id+"F0.wireOp",EDGE,"E52.2"),sQuery(id+"F0.wireOp",EDGE,"E52.3"),sQuery(id+"F0.wireOp",EDGE,"E52.4"),sQuery(id+"F0.wireOp",EDGE,"E52.5"),sQuery(id+"F0.wireOp",EDGE,"E54")])],"isStart":false}),makeQuery(id+"F4.opExtrude","SWEPT_FACE",FACE,{"disambiguationData":[OSD([sQuery(id+"F0.wireOp",EDGE,"E39")])]})]});
            var Q1;
            Q1=makeQuery(id+"F4.boolean.opBoolean","INTERSECT",EDGE,{"derivedFrom":[makeQuery(id+"F3.opExtrude","CAP_FACE",FACE,{"disambiguationData":[OSD([sQuery(id+"F0.wireOp",EDGE,"E1.bottom"),sQuery(id+"F0.wireOp",EDGE,"E2.left"),sQuery(id+"F0.wireOp",EDGE,"E25.left"),sQuery(id+"F0.wireOp",EDGE,"E25.right"),sQuery(id+"F0.wireOp",EDGE,"E27"),sQuery(id+"F0.wireOp",EDGE,"E28"),sQuery(id+"F0.wireOp",EDGE,"E30"),sQuery(id+"F0.wireOp",EDGE,"E31"),sQuery(id+"F0.wireOp",EDGE,"E32"),sQuery(id+"F0.wireOp",EDGE,"E33"),sQuery(id+"F0.wireOp",EDGE,"E34"),sQuery(id+"F0.wireOp",EDGE,"E36"),sQuery(id+"F0.wireOp",EDGE,"E37"),sQuery(id+"F0.wireOp",EDGE,"E38.1.0"),sQuery(id+"F0.wireOp",EDGE,"E38.1.1"),sQuery(id+"F0.wireOp",EDGE,"E38.1.2"),sQuery(id+"F0.wireOp",EDGE,"E38.1.3"),sQuery(id+"F0.wireOp",EDGE,"E38.1.4"),sQuery(id+"F0.wireOp",EDGE,"E47"),sQuery(id+"F0.wireOp",EDGE,"E48"),sQuery(id+"F0.wireOp",EDGE,"E49"),sQuery(id+"F0.wireOp",EDGE,"E50"),sQuery(id+"F0.wireOp",EDGE,"E52.0"),sQuery(id+"F0.wireOp",EDGE,"E52.1"),sQuery(id+"F0.wireOp",EDGE,"E52.2"),sQuery(id+"F0.wireOp",EDGE,"E52.3"),sQuery(id+"F0.wireOp",EDGE,"E52.4"),sQuery(id+"F0.wireOp",EDGE,"E52.5"),sQuery(id+"F0.wireOp",EDGE,"E54")])],"isStart":false}),makeQuery(id+"F4.opExtrude","SWEPT_FACE",FACE,{"disambiguationData":[OSD([sQuery(id+"F0.wireOp",EDGE,"E56.MirrorCS")])]})]});
            var Q2;
            {var subQ0=sQuery(id+"F0.wireOp",EDGE,"E54");Q2=makeQuery(id+"F4.boolean.opBoolean","INTERSECT",EDGE,{"disambiguationData":[OD(0.0)],"derivedFrom":[makeQuery(id+"F3.opExtrude","CAP_FACE",FACE,{"disambiguationData":[OSD([sQuery(id+"F0.wireOp",EDGE,"E1.bottom"),sQuery(id+"F0.wireOp",EDGE,"E2.left"),sQuery(id+"F0.wireOp",EDGE,"E25.left"),sQuery(id+"F0.wireOp",EDGE,"E25.right"),sQuery(id+"F0.wireOp",EDGE,"E27"),sQuery(id+"F0.wireOp",EDGE,"E28"),sQuery(id+"F0.wireOp",EDGE,"E30"),sQuery(id+"F0.wireOp",EDGE,"E31"),sQuery(id+"F0.wireOp",EDGE,"E32"),sQuery(id+"F0.wireOp",EDGE,"E33"),sQuery(id+"F0.wireOp",EDGE,"E34"),sQuery(id+"F0.wireOp",EDGE,"E36"),sQuery(id+"F0.wireOp",EDGE,"E37"),sQuery(id+"F0.wireOp",EDGE,"E38.1.0"),sQuery(id+"F0.wireOp",EDGE,"E38.1.1"),sQuery(id+"F0.wireOp",EDGE,"E38.1.2"),sQuery(id+"F0.wireOp",EDGE,"E38.1.3"),sQuery(id+"F0.wireOp",EDGE,"E38.1.4"),sQuery(id+"F0.wireOp",EDGE,"E47"),sQuery(id+"F0.wireOp",EDGE,"E48"),sQuery(id+"F0.wireOp",EDGE,"E49"),sQuery(id+"F0.wireOp",EDGE,"E50"),sQuery(id+"F0.wireOp",EDGE,"E52.0"),sQuery(id+"F0.wireOp",EDGE,"E52.1"),sQuery(id+"F0.wireOp",EDGE,"E52.2"),sQuery(id+"F0.wireOp",EDGE,"E52.3"),sQuery(id+"F0.wireOp",EDGE,"E52.4"),sQuery(id+"F0.wireOp",EDGE,"E52.5"),subQ0])],"isStart":false}),makeQuery(id+"F4.opExtrude","SWEPT_FACE",FACE,{"disambiguationData":[OSD([subQ0])]})]});}
            var Q3;
            Q3=makeQuery(id+"F4.boolean.opBoolean","INTERSECT",EDGE,{"derivedFrom":[makeQuery(id+"F3.opExtrude","CAP_FACE",FACE,{"disambiguationData":[OSD([sQuery(id+"F0.wireOp",EDGE,"E1.bottom"),sQuery(id+"F0.wireOp",EDGE,"E2.left"),sQuery(id+"F0.wireOp",EDGE,"E25.left"),sQuery(id+"F0.wireOp",EDGE,"E25.right"),sQuery(id+"F0.wireOp",EDGE,"E27"),sQuery(id+"F0.wireOp",EDGE,"E28"),sQuery(id+"F0.wireOp",EDGE,"E30"),sQuery(id+"F0.wireOp",EDGE,"E31"),sQuery(id+"F0.wireOp",EDGE,"E32"),sQuery(id+"F0.wireOp",EDGE,"E33"),sQuery(id+"F0.wireOp",EDGE,"E34"),sQuery(id+"F0.wireOp",EDGE,"E36"),sQuery(id+"F0.wireOp",EDGE,"E37"),sQuery(id+"F0.wireOp",EDGE,"E38.1.0"),sQuery(id+"F0.wireOp",EDGE,"E38.1.1"),sQuery(id+"F0.wireOp",EDGE,"E38.1.2"),sQuery(id+"F0.wireOp",EDGE,"E38.1.3"),sQuery(id+"F0.wireOp",EDGE,"E38.1.4"),sQuery(id+"F0.wireOp",EDGE,"E47"),sQuery(id+"F0.wireOp",EDGE,"E48"),sQuery(id+"F0.wireOp",EDGE,"E49"),sQuery(id+"F0.wireOp",EDGE,"E50"),sQuery(id+"F0.wireOp",EDGE,"E52.0"),sQuery(id+"F0.wireOp",EDGE,"E52.1"),sQuery(id+"F0.wireOp",EDGE,"E52.2"),sQuery(id+"F0.wireOp",EDGE,"E52.3"),sQuery(id+"F0.wireOp",EDGE,"E52.4"),sQuery(id+"F0.wireOp",EDGE,"E52.5"),sQuery(id+"F0.wireOp",EDGE,"E54")])],"isStart":false}),makeQuery(id+"F4.opExtrude","SWEPT_FACE",FACE,{"disambiguationData":[OSD([sQuery(id+"F0.wireOp",EDGE,"E55")])]})]});
            var Q4;
            {var subQ0=sQuery(id+"F0.wireOp",EDGE,"E54");Q4=makeQuery(id+"F4.boolean.opBoolean","INTERSECT",EDGE,{"disambiguationData":[OD(1.0)],"derivedFrom":[makeQuery(id+"F3.opExtrude","CAP_FACE",FACE,{"disambiguationData":[OSD([sQuery(id+"F0.wireOp",EDGE,"E1.bottom"),sQuery(id+"F0.wireOp",EDGE,"E2.left"),sQuery(id+"F0.wireOp",EDGE,"E25.left"),sQuery(id+"F0.wireOp",EDGE,"E25.right"),sQuery(id+"F0.wireOp",EDGE,"E27"),sQuery(id+"F0.wireOp",EDGE,"E28"),sQuery(id+"F0.wireOp",EDGE,"E30"),sQuery(id+"F0.wireOp",EDGE,"E31"),sQuery(id+"F0.wireOp",EDGE,"E32"),sQuery(id+"F0.wireOp",EDGE,"E33"),sQuery(id+"F0.wireOp",EDGE,"E34"),sQuery(id+"F0.wireOp",EDGE,"E36"),sQuery(id+"F0.wireOp",EDGE,"E37"),sQuery(id+"F0.wireOp",EDGE,"E38.1.0"),sQuery(id+"F0.wireOp",EDGE,"E38.1.1"),sQuery(id+"F0.wireOp",EDGE,"E38.1.2"),sQuery(id+"F0.wireOp",EDGE,"E38.1.3"),sQuery(id+"F0.wireOp",EDGE,"E38.1.4"),sQuery(id+"F0.wireOp",EDGE,"E47"),sQuery(id+"F0.wireOp",EDGE,"E48"),sQuery(id+"F0.wireOp",EDGE,"E49"),sQuery(id+"F0.wireOp",EDGE,"E50"),sQuery(id+"F0.wireOp",EDGE,"E52.0"),sQuery(id+"F0.wireOp",EDGE,"E52.1"),sQuery(id+"F0.wireOp",EDGE,"E52.2"),sQuery(id+"F0.wireOp",EDGE,"E52.3"),sQuery(id+"F0.wireOp",EDGE,"E52.4"),sQuery(id+"F0.wireOp",EDGE,"E52.5"),subQ0])],"isStart":false}),makeQuery(id+"F4.opExtrude","SWEPT_FACE",FACE,{"disambiguationData":[OSD([subQ0])]})]});}
            var Q5;
            Q5=makeQuery(id+"F4.boolean.opBoolean","INTERSECT",EDGE,{"derivedFrom":[makeQuery(id+"F3.opExtrude","CAP_FACE",FACE,{"disambiguationData":[OSD([sQuery(id+"F0.wireOp",EDGE,"E1.bottom"),sQuery(id+"F0.wireOp",EDGE,"E2.left"),sQuery(id+"F0.wireOp",EDGE,"E25.left"),sQuery(id+"F0.wireOp",EDGE,"E25.right"),sQuery(id+"F0.wireOp",EDGE,"E27"),sQuery(id+"F0.wireOp",EDGE,"E28"),sQuery(id+"F0.wireOp",EDGE,"E30"),sQuery(id+"F0.wireOp",EDGE,"E31"),sQuery(id+"F0.wireOp",EDGE,"E32"),sQuery(id+"F0.wireOp",EDGE,"E33"),sQuery(id+"F0.wireOp",EDGE,"E34"),sQuery(id+"F0.wireOp",EDGE,"E36"),sQuery(id+"F0.wireOp",EDGE,"E37"),sQuery(id+"F0.wireOp",EDGE,"E38.1.0"),sQuery(id+"F0.wireOp",EDGE,"E38.1.1"),sQuery(id+"F0.wireOp",EDGE,"E38.1.2"),sQuery(id+"F0.wireOp",EDGE,"E38.1.3"),sQuery(id+"F0.wireOp",EDGE,"E38.1.4"),sQuery(id+"F0.wireOp",EDGE,"E47"),sQuery(id+"F0.wireOp",EDGE,"E48"),sQuery(id+"F0.wireOp",EDGE,"E49"),sQuery(id+"F0.wireOp",EDGE,"E50"),sQuery(id+"F0.wireOp",EDGE,"E52.0"),sQuery(id+"F0.wireOp",EDGE,"E52.1"),sQuery(id+"F0.wireOp",EDGE,"E52.2"),sQuery(id+"F0.wireOp",EDGE,"E52.3"),sQuery(id+"F0.wireOp",EDGE,"E52.4"),sQuery(id+"F0.wireOp",EDGE,"E52.5"),sQuery(id+"F0.wireOp",EDGE,"E54")])],"isStart":false}),makeQuery(id+"F4.opExtrude","SWEPT_FACE",FACE,{"disambiguationData":[OSD([sQuery(id+"F0.wireOp",EDGE,"E40")])]})]});
            fillet(context, id + "F11", {"entities" : qUnion([Q0, Q1, Q2, Q3, Q4, Q5]), "radius" : 5 * mm, "tangentPropagation" : true, "allowEdgeOverflow" : false});
        }
        {
            var Q0;
            Q0=makeQuery(id+"F0.imprint","IMPRINT",FACE,{"disambiguationData":[TD([[makeQuery(id+"F0.imprint","IMPRINT",EDGE,{"derivedFrom":sQuery(id+"F0.wireOp",EDGE,"E44.bottom")}),-1.0]])]});
            extrude(context, id + "F12", {"entities" : qUnion([Q0]), "depth" : 80 * mm});
        }
        {
            var Q0;
            Q0=makeQuery(id+"F4.boolean.opBoolean","INTERSECT",EDGE,{"derivedFrom":[makeQuery(id+"F3.opExtrude","CAP_FACE",FACE,{"disambiguationData":[OSD([sQuery(id+"F0.wireOp",EDGE,"E1.bottom"),sQuery(id+"F0.wireOp",EDGE,"E2.left"),sQuery(id+"F0.wireOp",EDGE,"E25.left"),sQuery(id+"F0.wireOp",EDGE,"E25.right"),sQuery(id+"F0.wireOp",EDGE,"E27"),sQuery(id+"F0.wireOp",EDGE,"E28"),sQuery(id+"F0.wireOp",EDGE,"E30"),sQuery(id+"F0.wireOp",EDGE,"E31"),sQuery(id+"F0.wireOp",EDGE,"E32"),sQuery(id+"F0.wireOp",EDGE,"E33"),sQuery(id+"F0.wireOp",EDGE,"E34"),sQuery(id+"F0.wireOp",EDGE,"E36"),sQuery(id+"F0.wireOp",EDGE,"E37"),sQuery(id+"F0.wireOp",EDGE,"E38.1.0"),sQuery(id+"F0.wireOp",EDGE,"E38.1.1"),sQuery(id+"F0.wireOp",EDGE,"E38.1.2"),sQuery(id+"F0.wireOp",EDGE,"E38.1.3"),sQuery(id+"F0.wireOp",EDGE,"E38.1.4"),sQuery(id+"F0.wireOp",EDGE,"E47"),sQuery(id+"F0.wireOp",EDGE,"E48"),sQuery(id+"F0.wireOp",EDGE,"E49"),sQuery(id+"F0.wireOp",EDGE,"E50"),sQuery(id+"F0.wireOp",EDGE,"E52.0"),sQuery(id+"F0.wireOp",EDGE,"E52.1"),sQuery(id+"F0.wireOp",EDGE,"E52.2"),sQuery(id+"F0.wireOp",EDGE,"E52.3"),sQuery(id+"F0.wireOp",EDGE,"E52.4"),sQuery(id+"F0.wireOp",EDGE,"E52.5"),sQuery(id+"F0.wireOp",EDGE,"E54")])],"isStart":false}),makeQuery(id+"F4.opExtrude","SWEPT_FACE",FACE,{"disambiguationData":[OSD([sQuery(id+"F0.wireOp",EDGE,"E55")])]})]});
            var Q1;
            Q1=makeQuery(id+"F4.boolean.opBoolean","INTERSECT",EDGE,{"derivedFrom":[makeQuery(id+"F3.opExtrude","CAP_FACE",FACE,{"disambiguationData":[OSD([sQuery(id+"F0.wireOp",EDGE,"E1.bottom"),sQuery(id+"F0.wireOp",EDGE,"E2.left"),sQuery(id+"F0.wireOp",EDGE,"E25.left"),sQuery(id+"F0.wireOp",EDGE,"E25.right"),sQuery(id+"F0.wireOp",EDGE,"E27"),sQuery(id+"F0.wireOp",EDGE,"E28"),sQuery(id+"F0.wireOp",EDGE,"E30"),sQuery(id+"F0.wireOp",EDGE,"E31"),sQuery(id+"F0.wireOp",EDGE,"E32"),sQuery(id+"F0.wireOp",EDGE,"E33"),sQuery(id+"F0.wireOp",EDGE,"E34"),sQuery(id+"F0.wireOp",EDGE,"E36"),sQuery(id+"F0.wireOp",EDGE,"E37"),sQuery(id+"F0.wireOp",EDGE,"E38.1.0"),sQuery(id+"F0.wireOp",EDGE,"E38.1.1"),sQuery(id+"F0.wireOp",EDGE,"E38.1.2"),sQuery(id+"F0.wireOp",EDGE,"E38.1.3"),sQuery(id+"F0.wireOp",EDGE,"E38.1.4"),sQuery(id+"F0.wireOp",EDGE,"E47"),sQuery(id+"F0.wireOp",EDGE,"E48"),sQuery(id+"F0.wireOp",EDGE,"E49"),sQuery(id+"F0.wireOp",EDGE,"E50"),sQuery(id+"F0.wireOp",EDGE,"E52.0"),sQuery(id+"F0.wireOp",EDGE,"E52.1"),sQuery(id+"F0.wireOp",EDGE,"E52.2"),sQuery(id+"F0.wireOp",EDGE,"E52.3"),sQuery(id+"F0.wireOp",EDGE,"E52.4"),sQuery(id+"F0.wireOp",EDGE,"E52.5"),sQuery(id+"F0.wireOp",EDGE,"E54")])],"isStart":false}),makeQuery(id+"F4.opExtrude","SWEPT_FACE",FACE,{"disambiguationData":[OSD([sQuery(id+"F0.wireOp",EDGE,"E40")])]})]});
            var Q2;
            {var subQ0=sQuery(id+"F0.wireOp",EDGE,"E54");Q2=makeQuery(id+"F4.boolean.opBoolean","INTERSECT",EDGE,{"disambiguationData":[OD(1.0)],"derivedFrom":[makeQuery(id+"F3.opExtrude","CAP_FACE",FACE,{"disambiguationData":[OSD([sQuery(id+"F0.wireOp",EDGE,"E1.bottom"),sQuery(id+"F0.wireOp",EDGE,"E2.left"),sQuery(id+"F0.wireOp",EDGE,"E25.left"),sQuery(id+"F0.wireOp",EDGE,"E25.right"),sQuery(id+"F0.wireOp",EDGE,"E27"),sQuery(id+"F0.wireOp",EDGE,"E28"),sQuery(id+"F0.wireOp",EDGE,"E30"),sQuery(id+"F0.wireOp",EDGE,"E31"),sQuery(id+"F0.wireOp",EDGE,"E32"),sQuery(id+"F0.wireOp",EDGE,"E33"),sQuery(id+"F0.wireOp",EDGE,"E34"),sQuery(id+"F0.wireOp",EDGE,"E36"),sQuery(id+"F0.wireOp",EDGE,"E37"),sQuery(id+"F0.wireOp",EDGE,"E38.1.0"),sQuery(id+"F0.wireOp",EDGE,"E38.1.1"),sQuery(id+"F0.wireOp",EDGE,"E38.1.2"),sQuery(id+"F0.wireOp",EDGE,"E38.1.3"),sQuery(id+"F0.wireOp",EDGE,"E38.1.4"),sQuery(id+"F0.wireOp",EDGE,"E47"),sQuery(id+"F0.wireOp",EDGE,"E48"),sQuery(id+"F0.wireOp",EDGE,"E49"),sQuery(id+"F0.wireOp",EDGE,"E50"),sQuery(id+"F0.wireOp",EDGE,"E52.0"),sQuery(id+"F0.wireOp",EDGE,"E52.1"),sQuery(id+"F0.wireOp",EDGE,"E52.2"),sQuery(id+"F0.wireOp",EDGE,"E52.3"),sQuery(id+"F0.wireOp",EDGE,"E52.4"),sQuery(id+"F0.wireOp",EDGE,"E52.5"),subQ0])],"isStart":false}),makeQuery(id+"F4.opExtrude","SWEPT_FACE",FACE,{"disambiguationData":[OSD([subQ0])]})]});}
            var Q3;
            Q3=makeQuery(id+"F3.opExtrude","CAP_EDGE",EDGE,{"disambiguationData":[OSD([sQuery(id+"F0.wireOp",EDGE,"E50")])],"isStart":false});
            var Q4;
            Q4=makeQuery(id+"F3.opExtrude","CAP_EDGE",EDGE,{"disambiguationData":[OSD([sQuery(id+"F0.wireOp",EDGE,"E1.bottom"),sQuery(id+"F0.wireOp",EDGE,"E47")])],"isStart":false});
            var Q5;
            Q5=makeQuery(id+"F3.opExtrude","SWEPT_EDGE",EDGE,{"disambiguationData":[OSD([sQuery(id+"F0.wireOp",EDGE,"E47"),sQuery(id+"F0.wireOp",EDGE,"E50")])]});
            var Q6;
            Q6=makeQuery(id+"F9.opChamfer","BLEND_EDGE",EDGE,{"blendedFrom":[makeQuery(id+"F4.opExtrude","CAP_EDGE",EDGE,{"disambiguationData":[OSD([sQuery(id+"F0.wireOp",EDGE,"E107")])],"isStart":false}),makeQuery(id+"F4.opExtrude","SWEPT_FACE",FACE,{"disambiguationData":[OSD([sQuery(id+"F0.wireOp",EDGE,"E103")])]})],"blendedInto":[makeQuery(id+"F4.opExtrude","SWEPT_FACE",FACE,{"disambiguationData":[OSD([sQuery(id+"F0.wireOp",EDGE,"E103")])]})]});
            var Q7;
            Q7=makeQuery(id+"F9.opChamfer","BLEND_EDGE",EDGE,{"blendedFrom":[makeQuery(id+"F4.opExtrude","CAP_EDGE",EDGE,{"disambiguationData":[OSD([sQuery(id+"F0.wireOp",EDGE,"E107")])],"isStart":false}),makeQuery(id+"F4.opExtrude","SWEPT_FACE",FACE,{"disambiguationData":[OSD([sQuery(id+"F0.wireOp",EDGE,"E104.MirrorCS")])]})],"blendedInto":[makeQuery(id+"F4.opExtrude","SWEPT_FACE",FACE,{"disambiguationData":[OSD([sQuery(id+"F0.wireOp",EDGE,"E104.MirrorCS")])]})]});
            var Q8;
            Q8=makeQuery(id+"F4.opExtrude","CAP_EDGE",EDGE,{"disambiguationData":[OSD([sQuery(id+"F0.wireOp",EDGE,"E80")])],"isStart":false});
            var Q9;
            Q9=makeQuery(id+"F4.opExtrude","CAP_EDGE",EDGE,{"disambiguationData":[OSD([sQuery(id+"F0.wireOp",EDGE,"E103")])],"isStart":false});
            var Q10;
            Q10=makeQuery(id+"F4.opExtrude","CAP_EDGE",EDGE,{"disambiguationData":[OSD([sQuery(id+"F0.wireOp",EDGE,"E104.MirrorCS")])],"isStart":false});
            var Q11;
            Q11=makeQuery(id+"F4.opExtrude","CAP_EDGE",EDGE,{"disambiguationData":[OSD([sQuery(id+"F0.wireOp",EDGE,"E79")])],"isStart":false});
            var Q12;
            Q12=makeQuery(id+"F4.opExtrude","CAP_EDGE",EDGE,{"disambiguationData":[OSD([sQuery(id+"F0.wireOp",EDGE,"E95")])],"isStart":false});
            var Q13;
            Q13=makeQuery(id+"F4.opExtrude","SWEPT_EDGE",EDGE,{"disambiguationData":[OSD([sQuery(id+"F0.wireOp",EDGE,"E79"),sQuery(id+"F0.wireOp",EDGE,"E95"),sQuery(id+"F0.wireOp",EDGE,"E97")])]});
            var Q14;
            Q14=makeQuery(id+"F3.opExtrude","CAP_EDGE",EDGE,{"disambiguationData":[OSD([sQuery(id+"F0.wireOp",EDGE,"E95"),sQuery(id+"F0.wireOp",EDGE,"E97")])],"isStart":false});
            var Q15;
            Q15=makeQuery(id+"F3.opExtrude","CAP_EDGE",EDGE,{"disambiguationData":[OSD([sQuery(id+"F0.wireOp",EDGE,"E90")])],"isStart":false});
            var Q16;
            Q16=makeQuery(id+"F4.opExtrude","SWEPT_EDGE",EDGE,{"disambiguationData":[OSD([sQuery(id+"F0.wireOp",EDGE,"E66.bottom"),sQuery(id+"F0.wireOp",EDGE,"E80")])]});
            var Q17;
            Q17=makeQuery(id+"F3.opExtrude","CAP_EDGE",EDGE,{"disambiguationData":[OSD([sQuery(id+"F0.wireOp",EDGE,"E66.bottom")])],"isStart":false});
            var Q18;
            Q18=makeQuery(id+"F3.opExtrude","CAP_EDGE",EDGE,{"disambiguationData":[OSD([sQuery(id+"F0.wireOp",EDGE,"E91")])],"isStart":false});
            var Q19;
            Q19=makeQuery(id+"F3.opExtrude","SWEPT_EDGE",EDGE,{"disambiguationData":[OSD([sQuery(id+"F0.wireOp",EDGE,"E66.bottom"),sQuery(id+"F0.wireOp",EDGE,"E84"),sQuery(id+"F0.wireOp",EDGE,"E91")])]});
            var Q20;
            Q20=makeQuery(id+"F3.opExtrude","SWEPT_EDGE",EDGE,{"disambiguationData":[OSD([sQuery(id+"F0.wireOp",EDGE,"E86"),sQuery(id+"F0.wireOp",EDGE,"E91")])]});
            var Q21;
            Q21=makeQuery(id+"F3.opExtrude","CAP_EDGE",EDGE,{"disambiguationData":[OSD([sQuery(id+"F0.wireOp",EDGE,"E86")])],"isStart":false});
            var Q22;
            Q22=makeQuery(id+"F3.opExtrude","CAP_EDGE",EDGE,{"disambiguationData":[OSD([sQuery(id+"F0.wireOp",EDGE,"E85")])],"isStart":false});
            var Q23;
            Q23=makeQuery(id+"F6.opExtrude","CAP_EDGE",EDGE,{"disambiguationData":[OSD([sQuery(id+"F0.wireOp",EDGE,"E79")])],"isStart":false});
            var Q24;
            Q24=makeQuery(id+"F6.opExtrude","CAP_EDGE",EDGE,{"disambiguationData":[OSD([sQuery(id+"F0.wireOp",EDGE,"E104.MirrorCS")])],"isStart":false});
            var Q25;
            Q25=makeQuery(id+"F9.opChamfer","BLEND_EDGE",EDGE,{"blendedFrom":[makeQuery(id+"F6.opExtrude","CAP_EDGE",EDGE,{"disambiguationData":[OSD([sQuery(id+"F0.wireOp",EDGE,"E107")])],"isStart":false}),makeQuery(id+"F6.opExtrude","SWEPT_FACE",FACE,{"disambiguationData":[OSD([sQuery(id+"F0.wireOp",EDGE,"E104.MirrorCS")])]})],"blendedInto":[makeQuery(id+"F6.opExtrude","SWEPT_FACE",FACE,{"disambiguationData":[OSD([sQuery(id+"F0.wireOp",EDGE,"E104.MirrorCS")])]})]});
            var Q26;
            Q26=makeQuery(id+"F9.opChamfer","BLEND_EDGE",EDGE,{"blendedFrom":[makeQuery(id+"F6.opExtrude","CAP_EDGE",EDGE,{"disambiguationData":[OSD([sQuery(id+"F0.wireOp",EDGE,"E107")])],"isStart":false}),makeQuery(id+"F6.opExtrude","SWEPT_FACE",FACE,{"disambiguationData":[OSD([sQuery(id+"F0.wireOp",EDGE,"E103")])]})],"blendedInto":[makeQuery(id+"F6.opExtrude","SWEPT_FACE",FACE,{"disambiguationData":[OSD([sQuery(id+"F0.wireOp",EDGE,"E103")])]})]});
            var Q27;
            Q27=makeQuery(id+"F6.opExtrude","CAP_EDGE",EDGE,{"disambiguationData":[OSD([sQuery(id+"F0.wireOp",EDGE,"E80")])],"isStart":false});
            var Q28;
            Q28=makeQuery(id+"F6.opExtrude","CAP_EDGE",EDGE,{"disambiguationData":[OSD([sQuery(id+"F0.wireOp",EDGE,"E103")])],"isStart":false});
            var Q29;
            Q29=makeQuery(id+"F6.opExtrude","SWEPT_EDGE",EDGE,{"disambiguationData":[OSD([sQuery(id+"F0.wireOp",EDGE,"E79"),sQuery(id+"F0.wireOp",EDGE,"E95"),sQuery(id+"F0.wireOp",EDGE,"E97")])]});
            var Q30;
            Q30=makeQuery(id+"F6.opExtrude","SWEPT_EDGE",EDGE,{"disambiguationData":[OSD([sQuery(id+"F0.wireOp",EDGE,"E66.bottom"),sQuery(id+"F0.wireOp",EDGE,"E80")])]});
            fillet(context, id + "F13", {"entities" : qUnion([Q0, Q1, Q2, Q3, Q4, Q5, Q6, Q7, Q8, Q9, Q10, Q11, Q12, Q13, Q14, Q15, Q16, Q17, Q18, Q19, Q20, Q21, Q22, Q23, Q24, Q25, Q26, Q27, Q28, Q29, Q30]), "radius" : 2 * mm, "tangentPropagation" : true, "allowEdgeOverflow" : false});
        }
        {
            var Q0;
            Q0=makeQuery(id+"F4.boolean.opBoolean","INTERSECT",EDGE,{"derivedFrom":[makeQuery(id+"F3.opExtrude","CAP_FACE",FACE,{"disambiguationData":[OSD([sQuery(id+"F0.wireOp",EDGE,"E66.bottom"),sQuery(id+"F0.wireOp",EDGE,"E67.left"),sQuery(id+"F0.wireOp",EDGE,"E67.right"),sQuery(id+"F0.wireOp",EDGE,"E69"),sQuery(id+"F0.wireOp",EDGE,"E70"),sQuery(id+"F0.wireOp",EDGE,"E72"),sQuery(id+"F0.wireOp",EDGE,"E73"),sQuery(id+"F0.wireOp",EDGE,"E74"),sQuery(id+"F0.wireOp",EDGE,"E78.1.0"),sQuery(id+"F0.wireOp",EDGE,"E78.1.1"),sQuery(id+"F0.wireOp",EDGE,"E78.1.2"),sQuery(id+"F0.wireOp",EDGE,"E78.1.3"),sQuery(id+"F0.wireOp",EDGE,"E78.1.4"),sQuery(id+"F0.wireOp",EDGE,"E85"),sQuery(id+"F0.wireOp",EDGE,"E86"),sQuery(id+"F0.wireOp",EDGE,"E89"),sQuery(id+"F0.wireOp",EDGE,"E90"),sQuery(id+"F0.wireOp",EDGE,"E91"),sQuery(id+"F0.wireOp",EDGE,"E92"),sQuery(id+"F0.wireOp",EDGE,"E93"),sQuery(id+"F0.wireOp",EDGE,"E94"),sQuery(id+"F0.wireOp",EDGE,"E95"),sQuery(id+"F0.wireOp",EDGE,"E96"),sQuery(id+"F0.wireOp",EDGE,"E97"),sQuery(id+"F0.wireOp",EDGE,"E98"),sQuery(id+"F0.wireOp",EDGE,"E99"),sQuery(id+"F0.wireOp",EDGE,"E100"),sQuery(id+"F0.wireOp",EDGE,"E101"),sQuery(id+"F0.wireOp",EDGE,"E102")])],"isStart":false}),makeQuery(id+"F4.opExtrude","SWEPT_FACE",FACE,{"disambiguationData":[OSD([sQuery(id+"F0.wireOp",EDGE,"E103")])]})]});
            var Q1;
            Q1=makeQuery(id+"F4.boolean.opBoolean","INTERSECT",EDGE,{"derivedFrom":[makeQuery(id+"F3.opExtrude","CAP_FACE",FACE,{"disambiguationData":[OSD([sQuery(id+"F0.wireOp",EDGE,"E66.bottom"),sQuery(id+"F0.wireOp",EDGE,"E67.left"),sQuery(id+"F0.wireOp",EDGE,"E67.right"),sQuery(id+"F0.wireOp",EDGE,"E69"),sQuery(id+"F0.wireOp",EDGE,"E70"),sQuery(id+"F0.wireOp",EDGE,"E72"),sQuery(id+"F0.wireOp",EDGE,"E73"),sQuery(id+"F0.wireOp",EDGE,"E74"),sQuery(id+"F0.wireOp",EDGE,"E78.1.0"),sQuery(id+"F0.wireOp",EDGE,"E78.1.1"),sQuery(id+"F0.wireOp",EDGE,"E78.1.2"),sQuery(id+"F0.wireOp",EDGE,"E78.1.3"),sQuery(id+"F0.wireOp",EDGE,"E78.1.4"),sQuery(id+"F0.wireOp",EDGE,"E85"),sQuery(id+"F0.wireOp",EDGE,"E86"),sQuery(id+"F0.wireOp",EDGE,"E89"),sQuery(id+"F0.wireOp",EDGE,"E90"),sQuery(id+"F0.wireOp",EDGE,"E91"),sQuery(id+"F0.wireOp",EDGE,"E92"),sQuery(id+"F0.wireOp",EDGE,"E93"),sQuery(id+"F0.wireOp",EDGE,"E94"),sQuery(id+"F0.wireOp",EDGE,"E95"),sQuery(id+"F0.wireOp",EDGE,"E96"),sQuery(id+"F0.wireOp",EDGE,"E97"),sQuery(id+"F0.wireOp",EDGE,"E98"),sQuery(id+"F0.wireOp",EDGE,"E99"),sQuery(id+"F0.wireOp",EDGE,"E100"),sQuery(id+"F0.wireOp",EDGE,"E101"),sQuery(id+"F0.wireOp",EDGE,"E102")])],"isStart":false}),makeQuery(id+"F4.opExtrude","SWEPT_FACE",FACE,{"disambiguationData":[OSD([sQuery(id+"F0.wireOp",EDGE,"E80")])]})]});
            var Q2;
            Q2=makeQuery(id+"F4.boolean.opBoolean","INTERSECT",EDGE,{"derivedFrom":[makeQuery(id+"F3.opExtrude","CAP_FACE",FACE,{"disambiguationData":[OSD([sQuery(id+"F0.wireOp",EDGE,"E66.bottom"),sQuery(id+"F0.wireOp",EDGE,"E67.left"),sQuery(id+"F0.wireOp",EDGE,"E67.right"),sQuery(id+"F0.wireOp",EDGE,"E69"),sQuery(id+"F0.wireOp",EDGE,"E70"),sQuery(id+"F0.wireOp",EDGE,"E72"),sQuery(id+"F0.wireOp",EDGE,"E73"),sQuery(id+"F0.wireOp",EDGE,"E74"),sQuery(id+"F0.wireOp",EDGE,"E78.1.0"),sQuery(id+"F0.wireOp",EDGE,"E78.1.1"),sQuery(id+"F0.wireOp",EDGE,"E78.1.2"),sQuery(id+"F0.wireOp",EDGE,"E78.1.3"),sQuery(id+"F0.wireOp",EDGE,"E78.1.4"),sQuery(id+"F0.wireOp",EDGE,"E85"),sQuery(id+"F0.wireOp",EDGE,"E86"),sQuery(id+"F0.wireOp",EDGE,"E89"),sQuery(id+"F0.wireOp",EDGE,"E90"),sQuery(id+"F0.wireOp",EDGE,"E91"),sQuery(id+"F0.wireOp",EDGE,"E92"),sQuery(id+"F0.wireOp",EDGE,"E93"),sQuery(id+"F0.wireOp",EDGE,"E94"),sQuery(id+"F0.wireOp",EDGE,"E95"),sQuery(id+"F0.wireOp",EDGE,"E96"),sQuery(id+"F0.wireOp",EDGE,"E97"),sQuery(id+"F0.wireOp",EDGE,"E98"),sQuery(id+"F0.wireOp",EDGE,"E99"),sQuery(id+"F0.wireOp",EDGE,"E100"),sQuery(id+"F0.wireOp",EDGE,"E101"),sQuery(id+"F0.wireOp",EDGE,"E102")])],"isStart":false}),makeQuery(id+"F4.opExtrude","SWEPT_FACE",FACE,{"disambiguationData":[OSD([sQuery(id+"F0.wireOp",EDGE,"E79")])]})]});
            var Q3;
            Q3=makeQuery(id+"F6.boolean.opBoolean","INTERSECT",EDGE,{"derivedFrom":[makeQuery(id+"F3.opExtrude","CAP_FACE",FACE,{"disambiguationData":[OSD([sQuery(id+"F0.wireOp",EDGE,"E66.bottom"),sQuery(id+"F0.wireOp",EDGE,"E67.left"),sQuery(id+"F0.wireOp",EDGE,"E67.right"),sQuery(id+"F0.wireOp",EDGE,"E69"),sQuery(id+"F0.wireOp",EDGE,"E70"),sQuery(id+"F0.wireOp",EDGE,"E72"),sQuery(id+"F0.wireOp",EDGE,"E73"),sQuery(id+"F0.wireOp",EDGE,"E74"),sQuery(id+"F0.wireOp",EDGE,"E78.1.0"),sQuery(id+"F0.wireOp",EDGE,"E78.1.1"),sQuery(id+"F0.wireOp",EDGE,"E78.1.2"),sQuery(id+"F0.wireOp",EDGE,"E78.1.3"),sQuery(id+"F0.wireOp",EDGE,"E78.1.4"),sQuery(id+"F0.wireOp",EDGE,"E85"),sQuery(id+"F0.wireOp",EDGE,"E86"),sQuery(id+"F0.wireOp",EDGE,"E89"),sQuery(id+"F0.wireOp",EDGE,"E90"),sQuery(id+"F0.wireOp",EDGE,"E91"),sQuery(id+"F0.wireOp",EDGE,"E92"),sQuery(id+"F0.wireOp",EDGE,"E93"),sQuery(id+"F0.wireOp",EDGE,"E94"),sQuery(id+"F0.wireOp",EDGE,"E95"),sQuery(id+"F0.wireOp",EDGE,"E96"),sQuery(id+"F0.wireOp",EDGE,"E97"),sQuery(id+"F0.wireOp",EDGE,"E98"),sQuery(id+"F0.wireOp",EDGE,"E99"),sQuery(id+"F0.wireOp",EDGE,"E100"),sQuery(id+"F0.wireOp",EDGE,"E101"),sQuery(id+"F0.wireOp",EDGE,"E102")])],"isStart":false}),makeQuery(id+"F6.opExtrude","SWEPT_FACE",FACE,{"disambiguationData":[OSD([sQuery(id+"F0.wireOp",EDGE,"E103")])]})]});
            var Q4;
            Q4=makeQuery(id+"F6.boolean.opBoolean","INTERSECT",EDGE,{"derivedFrom":[makeQuery(id+"F3.opExtrude","CAP_FACE",FACE,{"disambiguationData":[OSD([sQuery(id+"F0.wireOp",EDGE,"E66.bottom"),sQuery(id+"F0.wireOp",EDGE,"E67.left"),sQuery(id+"F0.wireOp",EDGE,"E67.right"),sQuery(id+"F0.wireOp",EDGE,"E69"),sQuery(id+"F0.wireOp",EDGE,"E70"),sQuery(id+"F0.wireOp",EDGE,"E72"),sQuery(id+"F0.wireOp",EDGE,"E73"),sQuery(id+"F0.wireOp",EDGE,"E74"),sQuery(id+"F0.wireOp",EDGE,"E78.1.0"),sQuery(id+"F0.wireOp",EDGE,"E78.1.1"),sQuery(id+"F0.wireOp",EDGE,"E78.1.2"),sQuery(id+"F0.wireOp",EDGE,"E78.1.3"),sQuery(id+"F0.wireOp",EDGE,"E78.1.4"),sQuery(id+"F0.wireOp",EDGE,"E85"),sQuery(id+"F0.wireOp",EDGE,"E86"),sQuery(id+"F0.wireOp",EDGE,"E89"),sQuery(id+"F0.wireOp",EDGE,"E90"),sQuery(id+"F0.wireOp",EDGE,"E91"),sQuery(id+"F0.wireOp",EDGE,"E92"),sQuery(id+"F0.wireOp",EDGE,"E93"),sQuery(id+"F0.wireOp",EDGE,"E94"),sQuery(id+"F0.wireOp",EDGE,"E95"),sQuery(id+"F0.wireOp",EDGE,"E96"),sQuery(id+"F0.wireOp",EDGE,"E97"),sQuery(id+"F0.wireOp",EDGE,"E98"),sQuery(id+"F0.wireOp",EDGE,"E99"),sQuery(id+"F0.wireOp",EDGE,"E100"),sQuery(id+"F0.wireOp",EDGE,"E101"),sQuery(id+"F0.wireOp",EDGE,"E102")])],"isStart":false}),makeQuery(id+"F6.opExtrude","SWEPT_FACE",FACE,{"disambiguationData":[OSD([sQuery(id+"F0.wireOp",EDGE,"E80")])]})]});
            var Q5;
            Q5=makeQuery(id+"F6.boolean.opBoolean","INTERSECT",EDGE,{"derivedFrom":[makeQuery(id+"F3.opExtrude","CAP_FACE",FACE,{"disambiguationData":[OSD([sQuery(id+"F0.wireOp",EDGE,"E66.bottom"),sQuery(id+"F0.wireOp",EDGE,"E67.left"),sQuery(id+"F0.wireOp",EDGE,"E67.right"),sQuery(id+"F0.wireOp",EDGE,"E69"),sQuery(id+"F0.wireOp",EDGE,"E70"),sQuery(id+"F0.wireOp",EDGE,"E72"),sQuery(id+"F0.wireOp",EDGE,"E73"),sQuery(id+"F0.wireOp",EDGE,"E74"),sQuery(id+"F0.wireOp",EDGE,"E78.1.0"),sQuery(id+"F0.wireOp",EDGE,"E78.1.1"),sQuery(id+"F0.wireOp",EDGE,"E78.1.2"),sQuery(id+"F0.wireOp",EDGE,"E78.1.3"),sQuery(id+"F0.wireOp",EDGE,"E78.1.4"),sQuery(id+"F0.wireOp",EDGE,"E85"),sQuery(id+"F0.wireOp",EDGE,"E86"),sQuery(id+"F0.wireOp",EDGE,"E89"),sQuery(id+"F0.wireOp",EDGE,"E90"),sQuery(id+"F0.wireOp",EDGE,"E91"),sQuery(id+"F0.wireOp",EDGE,"E92"),sQuery(id+"F0.wireOp",EDGE,"E93"),sQuery(id+"F0.wireOp",EDGE,"E94"),sQuery(id+"F0.wireOp",EDGE,"E95"),sQuery(id+"F0.wireOp",EDGE,"E96"),sQuery(id+"F0.wireOp",EDGE,"E97"),sQuery(id+"F0.wireOp",EDGE,"E98"),sQuery(id+"F0.wireOp",EDGE,"E99"),sQuery(id+"F0.wireOp",EDGE,"E100"),sQuery(id+"F0.wireOp",EDGE,"E101"),sQuery(id+"F0.wireOp",EDGE,"E102")])],"isStart":false}),makeQuery(id+"F6.opExtrude","SWEPT_FACE",FACE,{"disambiguationData":[OSD([sQuery(id+"F0.wireOp",EDGE,"E79")])]})]});
            fillet(context, id + "F14", {"entities" : qUnion([Q0, Q1, Q2, Q3, Q4, Q5]), "radius" : 5 * mm, "tangentPropagation" : true, "allowEdgeOverflow" : false});
        }
    });
